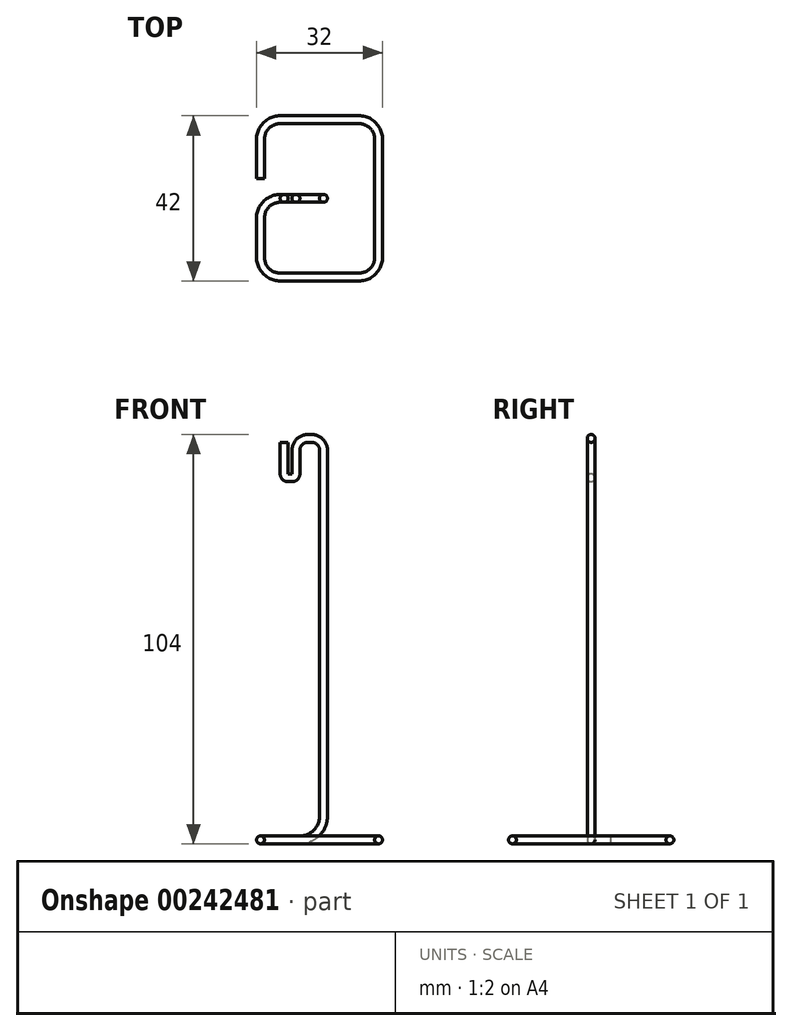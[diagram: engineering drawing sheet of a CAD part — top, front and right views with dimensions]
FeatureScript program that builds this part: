
annotation { "Feature Type Name" : "Feature", "Feature Type Description" : "" }
export const myFeature = defineFeature(function(context is Context, id is Id, definition is map)
    precondition{}
    {
        {
            var Q0;
            Q0=qCreatedBy(makeId("Front.planeOp"),FACE);
            var sketch = newSketch(context, id + "F0", { "sketchPlane" : qUnion([Q0])});
            skLineSegment(sketch, "E0", {"start": v(27.92, 5) * mm, "end": v(27.92, 98) * mm});
            skLineSegment(sketch, "E1", {"start": v(25.92, 100) * mm, "end": v(24.92, 100) * mm});
            skLineSegment(sketch, "E2", {"start": v(22.92, 98) * mm, "end": v(22.92, 92) * mm});
            skLineSegment(sketch, "E3", {"start": v(20.92, 90) * mm, "end": v(19.92, 90) * mm});
            skLineSegment(sketch, "E4", {"start": v(17.92, 92) * mm, "end": v(17.92, 100) * mm});
            skPoint(sketch, "E5.visualSharp", {"position": v(17.92, 90) * mm});
            skArc(sketch, "E5.filletArc", {"start": v(17.92, 92) * mm, "mid": v(18.5, 90.59) * mm, "end": v(19.92, 90) * mm});
            skPoint(sketch, "E6.visualSharp", {"position": v(22.92, 90) * mm});
            skArc(sketch, "E6.filletArc", {"start": v(20.92, 90) * mm, "mid": v(22.34, 90.59) * mm, "end": v(22.92, 92) * mm});
            skPoint(sketch, "E7.visualSharp", {"position": v(22.92, 100) * mm});
            skArc(sketch, "E7.filletArc", {"start": v(24.92, 100) * mm, "mid": v(23.5, 99.41) * mm, "end": v(22.92, 98) * mm});
            skPoint(sketch, "E8.visualSharp", {"position": v(27.92, 100) * mm});
            skArc(sketch, "E8.filletArc", {"start": v(27.92, 98) * mm, "mid": v(27.34, 99.41) * mm, "end": v(25.92, 100) * mm});
            skLineSegment(sketch, "E9", {"start": v(22.92, 0) * mm, "end": v(22.92, 0) * mm});
            skPoint(sketch, "E10.visualSharp", {"position": v(27.92, 0) * mm});
            skArc(sketch, "E10.filletArc", {"start": v(22.92, 0) * mm, "mid": v(26.46, 1.46) * mm, "end": v(27.92, 5) * mm});
            skSolve(sketch);
        }
        {
            var Q0;
            Q0=qCreatedBy(makeId("Top.planeOp"),FACE);
            var Q1;
            Q1=sQuery(id+"F0.wireOp",VERTEX,"E4.end");
            cPlane(context, id + "F1", {"entities" : qUnion([Q0, Q1]), "cplaneType" : CPlaneType.PLANE_POINT, "offset" : 25 * mm, "width" : 150 * mm, "height" : 150 * mm});
        }
        {
            var Q0;
            Q0=qCreatedBy(id+"F1.planeOp",FACE);
            var sketch = newSketch(context, id + "F2", { "sketchPlane" : qUnion([Q0])});
            skPoint(sketch, "E11.0", {"position": v(17.92, 0) * mm});
            skCircle(sketch, "E12", {"center": v(18.92, 0) * mm, "radius": 1 * mm});
            skSolve(sketch);
        }
        {
            var Q0;
            Q0=makeQuery(id+"F2.imprint","IMPRINT",FACE,{"disambiguationData":[TD([[makeQuery(id+"F2.imprint","IMPRINT",EDGE,{"derivedFrom":sQuery(id+"F2.wireOp",EDGE,"E12")}),1.0]])]});
            var Q1;
            Q1=sQuery(id+"F0.wireOp",EDGE,"E4");
            var Q2;
            Q2=sQuery(id+"F0.wireOp",EDGE,"E5.filletArc");
            var Q3;
            Q3=sQuery(id+"F0.wireOp",EDGE,"E3");
            var Q4;
            Q4=sQuery(id+"F0.wireOp",EDGE,"E6.filletArc");
            var Q5;
            Q5=sQuery(id+"F0.wireOp",EDGE,"E2");
            var Q6;
            Q6=sQuery(id+"F0.wireOp",EDGE,"E7.filletArc");
            var Q7;
            Q7=sQuery(id+"F0.wireOp",EDGE,"E1");
            var Q8;
            Q8=sQuery(id+"F0.wireOp",EDGE,"E8.filletArc");
            var Q9;
            Q9=sQuery(id+"F0.wireOp",EDGE,"E0");
            var Q10;
            Q10=sQuery(id+"F0.wireOp",EDGE,"E10.filletArc");
            sweep(context, id + "F3", {"profiles" : qUnion([Q0]), "path" : qUnion([Q1, Q2, Q3, Q4, Q5, Q6, Q7, Q8, Q9, Q10])});
        }
        {
            var Q0;
            Q0=qCreatedBy(makeId("Top.planeOp"),FACE);
            var sketch = newSketch(context, id + "F4", { "sketchPlane" : qUnion([Q0])});
            skLineSegment(sketch, "E13.0", {"start": v(22.92, 0) * mm, "end": v(27.92, 0) * mm, "construction": true});
            skLineSegment(sketch, "E14", {"start": v(12.92, -5) * mm, "end": v(12.92, -15) * mm});
            skLineSegment(sketch, "E15", {"start": v(17.92, -20) * mm, "end": v(37.92, -20) * mm});
            skLineSegment(sketch, "E16", {"start": v(42.92, -15) * mm, "end": v(42.92, 15) * mm});
            skLineSegment(sketch, "E17", {"start": v(37.92, 20) * mm, "end": v(17.92, 20) * mm});
            skLineSegment(sketch, "E18", {"start": v(12.92, 15) * mm, "end": v(12.92, 5) * mm});
            skPoint(sketch, "E19.visualSharp", {"position": v(12.92, 0) * mm});
            skArc(sketch, "E19.filletArc", {"start": v(17.92, 0) * mm, "mid": v(14.39, -1.46) * mm, "end": v(12.92, -5) * mm});
            skPoint(sketch, "E20.visualSharp", {"position": v(12.92, -20) * mm});
            skArc(sketch, "E20.filletArc", {"start": v(12.92, -15) * mm, "mid": v(14.39, -18.54) * mm, "end": v(17.92, -20) * mm});
            skPoint(sketch, "E21.visualSharp", {"position": v(12.92, 20) * mm});
            skArc(sketch, "E21.filletArc", {"start": v(17.92, 20) * mm, "mid": v(14.39, 18.54) * mm, "end": v(12.92, 15) * mm});
            skPoint(sketch, "E22.visualSharp", {"position": v(42.92, 20) * mm});
            skArc(sketch, "E22.filletArc", {"start": v(42.92, 15) * mm, "mid": v(41.46, 18.54) * mm, "end": v(37.92, 20) * mm});
            skPoint(sketch, "E23.visualSharp", {"position": v(42.92, -20) * mm});
            skArc(sketch, "E23.filletArc", {"start": v(37.92, -20) * mm, "mid": v(41.46, -18.54) * mm, "end": v(42.92, -15) * mm});
            skLineSegment(sketch, "E24", {"start": v(22.92, 0) * mm, "end": v(17.92, 0) * mm});
            skSolve(sketch);
        }
        {
            var Q0;
            Q0=makeQuery(id+"F3.opSweep","CAP_FACE",FACE,{"disambiguationData":[OSD([sQuery(id+"F0.wireOp",VERTEX,"E10.filletArc.start"),sQuery(id+"F2.wireOp",EDGE,"E12")])],"isStart":false});
            var Q1;
            Q1=sQuery(id+"F4.wireOp",EDGE,"E24");
            var Q2;
            Q2=sQuery(id+"F4.wireOp",EDGE,"E19.filletArc");
            var Q3;
            Q3=sQuery(id+"F4.wireOp",EDGE,"E14");
            var Q4;
            Q4=sQuery(id+"F4.wireOp",EDGE,"E20.filletArc");
            var Q5;
            Q5=sQuery(id+"F4.wireOp",EDGE,"E15");
            var Q6;
            Q6=sQuery(id+"F4.wireOp",EDGE,"E23.filletArc");
            var Q7;
            Q7=sQuery(id+"F4.wireOp",EDGE,"E16");
            var Q8;
            Q8=sQuery(id+"F4.wireOp",EDGE,"E22.filletArc");
            var Q9;
            Q9=sQuery(id+"F4.wireOp",EDGE,"E17");
            var Q10;
            Q10=sQuery(id+"F4.wireOp",EDGE,"E21.filletArc");
            var Q11;
            Q11=sQuery(id+"F4.wireOp",EDGE,"E18");
            sweep(context, id + "F5", {"operationType" : NewBodyOperationType.ADD, "profiles" : qUnion([Q0]), "path" : qUnion([Q1, Q2, Q3, Q4, Q5, Q6, Q7, Q8, Q9, Q10, Q11])});
        }
    });
